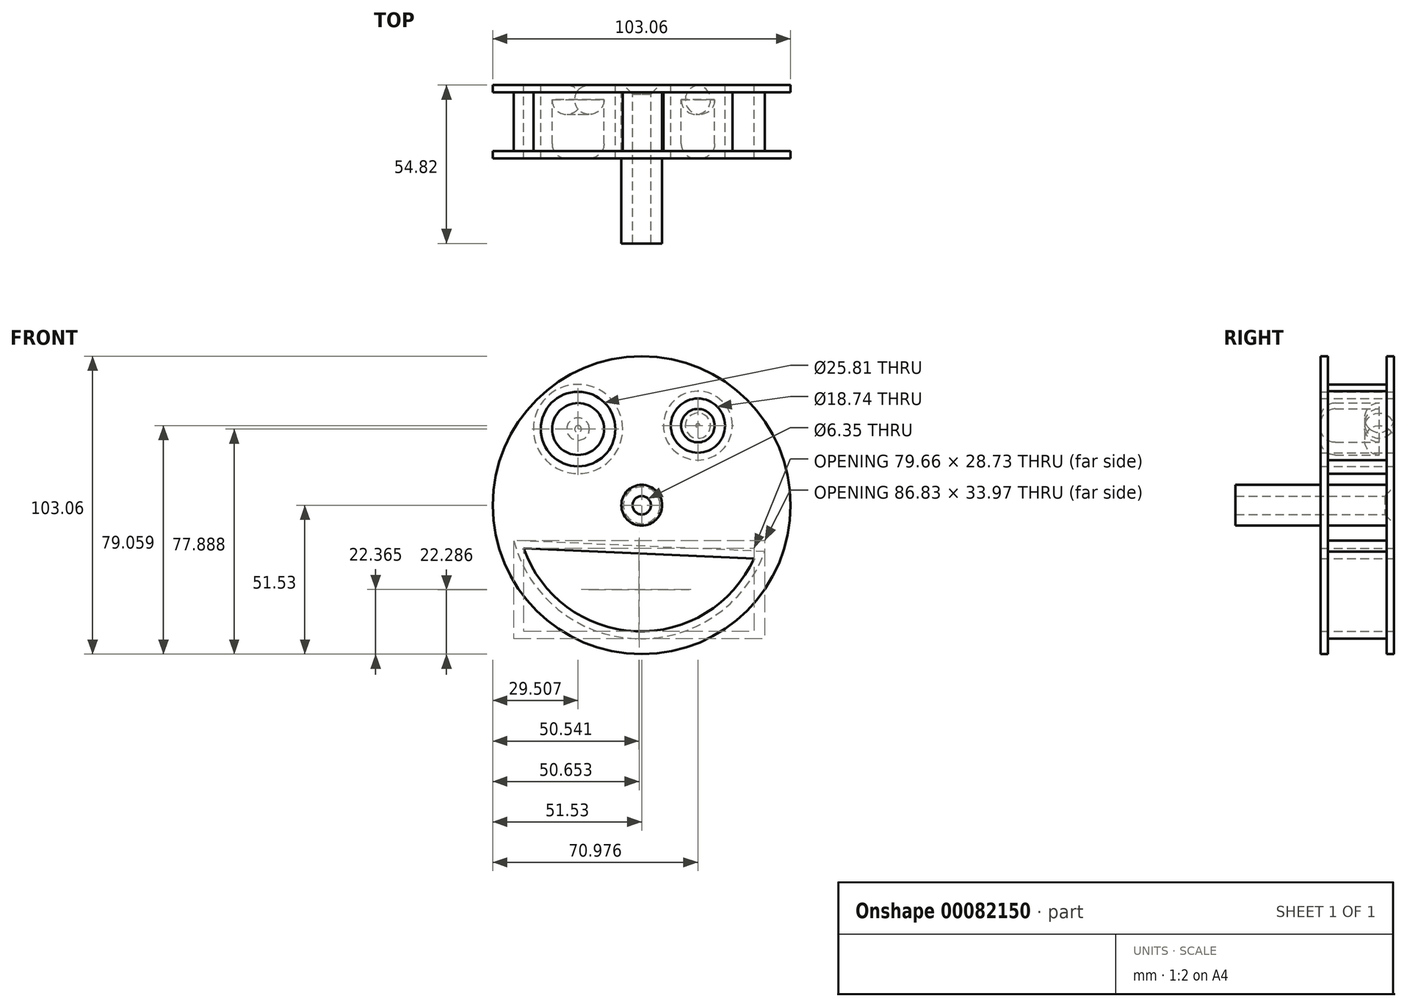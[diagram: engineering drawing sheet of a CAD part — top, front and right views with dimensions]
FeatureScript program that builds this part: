
annotation { "Feature Type Name" : "Feature", "Feature Type Description" : "" }
export const myFeature = defineFeature(function(context is Context, id is Id, definition is map)
    precondition{}
    {
        {
            var Q0;
            Q0=qCreatedBy(makeId("Front.planeOp"),FACE);
            var sketch = newSketch(context, id + "F0", { "sketchPlane" : qUnion([Q0])});
            skCircle(sketch, "E0", {"center": v(0, 0) * mm, "radius": 51.53 * mm});
            skCircle(sketch, "E1", {"center": v(-22.02, 26.36) * mm, "radius": 12.9 * mm});
            skCircle(sketch, "E2", {"center": v(19.45, 27.53) * mm, "radius": 5.79 * mm});
            skCircle(sketch, "E3", {"center": v(-22.02, 26.36) * mm, "radius": 8.98 * mm});
            skCircle(sketch, "E4", {"center": v(19.45, 27.53) * mm, "radius": 9.37 * mm});
            skArc(sketch, "E5", {"start": v(-40.82, -14.88) * mm, "mid": v(-2.18, -43.61) * mm, "end": v(38.84, -18.4) * mm});
            skLineSegment(sketch, "E6", {"start": v(38.84, -18.4) * mm, "end": v(-40.82, -14.88) * mm});
            skSolve(sketch);
        }
        {
            var Q0;
            Q0=makeQuery(id+"F0.imprint","IMPRINT",FACE,{"disambiguationData":[TD([[makeQuery(id+"F0.imprint","IMPRINT",EDGE,{"derivedFrom":sQuery(id+"F0.wireOp",EDGE,"E3")}),1.0]])]});
            var Q1;
            Q1=makeQuery(id+"F0.imprint","IMPRINT",FACE,{"disambiguationData":[TD([[makeQuery(id+"F0.imprint","IMPRINT",EDGE,{"derivedFrom":sQuery(id+"F0.wireOp",EDGE,"E2")}),1.0]])]});
            var Q2;
            Q2=makeQuery(id+"F0.imprint","IMPRINT",FACE,{"disambiguationData":[TD([[makeQuery(id+"F0.imprint","IMPRINT",EDGE,{"derivedFrom":sQuery(id+"F0.wireOp",EDGE,"E0")}),1.0]])]});
            extrude(context, id + "F1", {"entities" : qUnion([Q0, Q1, Q2]), "depth" : 25.4 * mm});
        }
        {
            var Q0;
            Q0=makeQuery(id+"F1.opExtrude","CAP_EDGE",EDGE,{"disambiguationData":[OSD([sQuery(id+"F0.wireOp",EDGE,"E3")])],"isStart":false});
            var Q1;
            Q1=makeQuery(id+"F1.opExtrude","CAP_FACE",FACE,{"disambiguationData":[OSD([sQuery(id+"F0.wireOp",EDGE,"E2")])],"isStart":false});
            var Q2;
            Q2=makeQuery(id+"F1.opExtrude","CAP_FACE",FACE,{"disambiguationData":[OSD([sQuery(id+"F0.wireOp",EDGE,"E3")])],"isStart":true});
            var Q3;
            Q3=makeQuery(id+"F1.opExtrude","CAP_FACE",FACE,{"disambiguationData":[OSD([sQuery(id+"F0.wireOp",EDGE,"E2")])],"isStart":true});
            fillet(context, id + "F2", {"entities" : qUnion([Q0, Q1, Q2, Q3]), "radius" : 5.08 * mm, "tangentPropagation" : true, "allowEdgeOverflow" : false});
        }
        {
            var Q0;
            Q0=makeQuery(id+"F1.opExtrude","SWEPT_FACE",FACE,{"disambiguationData":[OSD([sQuery(id+"F0.wireOp",EDGE,"E0")])]});
            shell(context, id + "F3", {"entities" : qUnion([Q0]), "thickness" : 2.54 * mm});
        }
        {
            var Q0;
            Q0=qCreatedBy(makeId("Front.planeOp"),FACE);
            var sketch = newSketch(context, id + "F4", { "sketchPlane" : qUnion([Q0])});
            skCircle(sketch, "E7", {"center": v(0, 0) * mm, "radius": 7.05 * mm});
            skSolve(sketch);
        }
        {
            var Q0;
            Q0 = qSketchRegion(id + "F4", true);
            extrude(context, id + "F5", {"entities" : qUnion([Q0]), "operationType" : NewBodyOperationType.ADD, "depth" : 54.82 * mm});
        }
        {
            var Q0;
            Q0=qCreatedBy(makeId("Front.planeOp"),FACE);
            var sketch = newSketch(context, id + "F6", { "sketchPlane" : qUnion([Q0])});
            skCircle(sketch, "E8", {"center": v(0, 0) * mm, "radius": 4.35 * mm});
            skSolve(sketch);
        }
        {
            var Q0;
            Q0=sQuery(id+"F6.wireOp",VERTEX,"E8.center");
            var Q1;
            Q1=makeQuery(id+"F1.opExtrude","SWEPT_BODY",BODY,{"disambiguationData":[OSD([sQuery(id+"F0.wireOp",EDGE,"E0"),sQuery(id+"F0.wireOp",EDGE,"E1"),sQuery(id+"F0.wireOp",EDGE,"E4"),sQuery(id+"F0.wireOp",EDGE,"E5"),sQuery(id+"F0.wireOp",EDGE,"E6")])]});
            hole(context, id + "F7", {"style" : HoleStyle.C_SINK, "endStyle" : HoleEndStyle.THROUGH, "oppositeDirection" : true, "holeDiameter" : 6.35 * mm, "cSinkDiameter" : 12.7 * mm, "cSinkAngle" : 90 * degree, "startFromSketch" : true, "locations" : qUnion([Q0]), "scope" : qUnion([Q1]), "isTappedThrough" : true});
        }
    });
